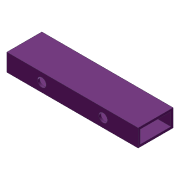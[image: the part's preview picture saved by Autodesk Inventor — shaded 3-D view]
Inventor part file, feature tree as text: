
AUTODESK INVENTOR PART (.ipt)
format: ipt  version: 2012 (Build 160160000, 160)  size: 102,912 bytes
history: native  units: in
note: dims shown in document units (in); Inventor stores cm internally (conversion verified against a paired STEP export)
features: extrude x3, sketch x3, shell x1
ambient origin geometry x8: Origin, YZ Plane, XZ Plane, XY Plane, X Axis, Y Axis, Z Axis, Center Point
bodies: Solid1 (feature_tree)
feature tree (7):
  extrude  "Extrusion1"  Depth=1.0in
  shell  "Shell1"  Thickness=2.0in
  extrude  "Extrusion2"  Depth=2.0in
  extrude  "Extrusion3"  Depth=0.5in
  sketch  "Sketch1"  dims[d0=7.5in d1=1.0in d2=2.0in d3=0.0in]
  sketch  "Sketch4"  dims[d4=0.125in d5=2.0in]
  sketch  "Sketch5"  dims[d6=2.0in d7=0.5in d8=0.5in d9=0.25in d10=1.0in d11=0.0in d12=0.5in d13=0.5in d14=1.0in d15=0.0in]
